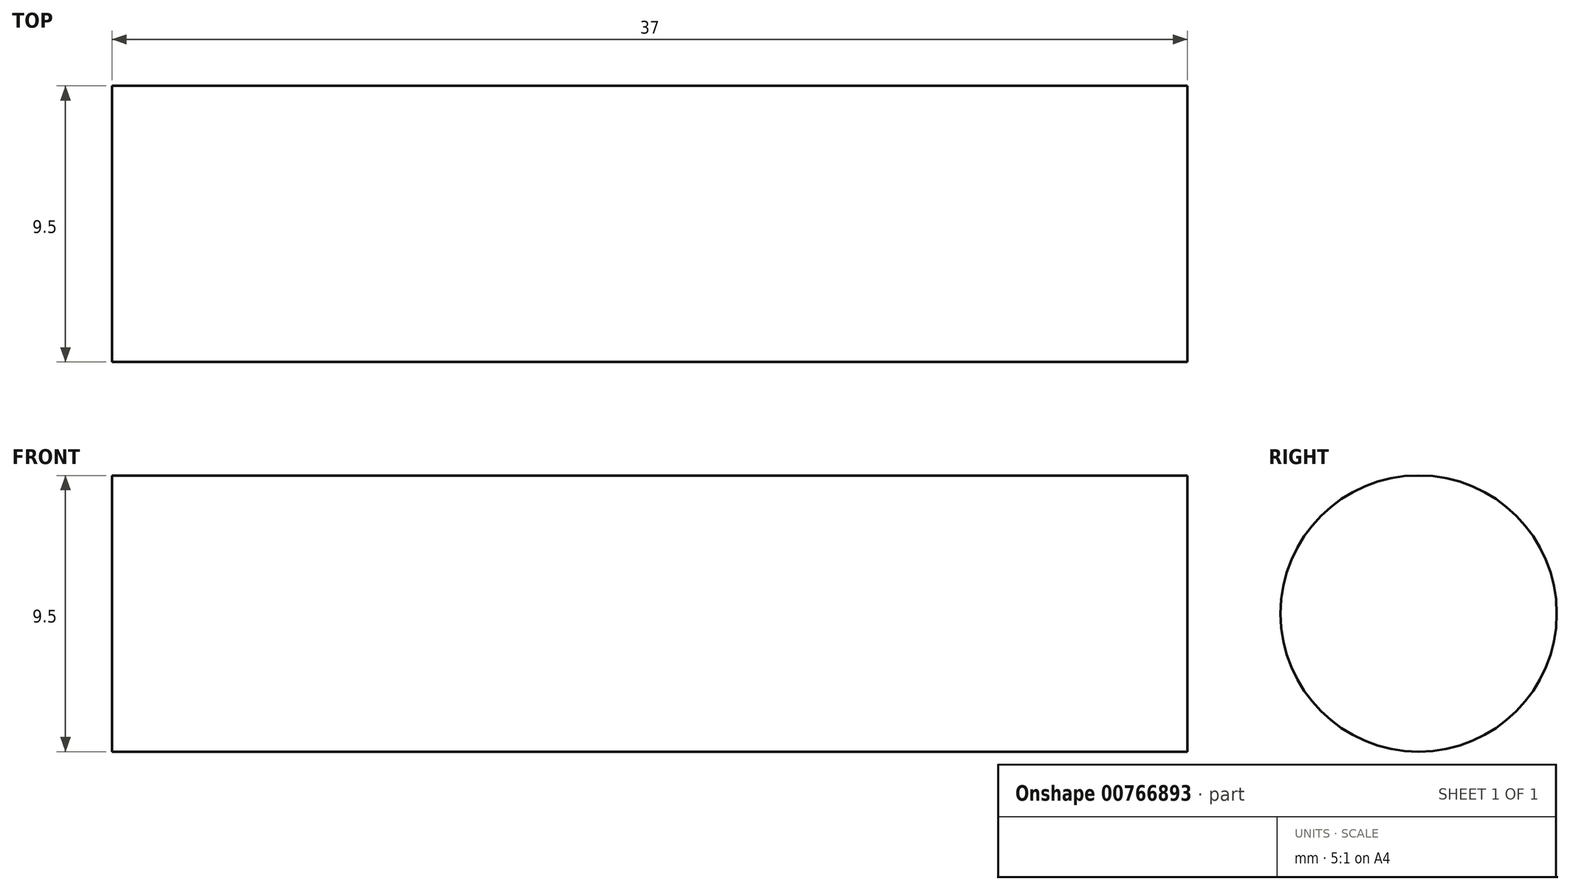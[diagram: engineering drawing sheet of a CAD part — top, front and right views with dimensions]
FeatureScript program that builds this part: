
annotation { "Feature Type Name" : "Feature", "Feature Type Description" : "" }
export const myFeature = defineFeature(function(context is Context, id is Id, definition is map)
    precondition{}
    {
        {
            var Q0;
            Q0=qCreatedBy(makeId("Right.planeOp"),FACE);
            var sketch = newSketch(context, id + "F0", { "sketchPlane" : qUnion([Q0])});
            skCircle(sketch, "E0", {"center": v(0, 0) * mm, "radius": 4.75 * mm});
            skSolve(sketch);
        }
        {
            var Q0;
            Q0=makeQuery(id+"F0.imprint","IMPRINT",FACE,{"disambiguationData":[TD([[makeQuery(id+"F0.imprint","IMPRINT",EDGE,{"derivedFrom":sQuery(id+"F0.wireOp",EDGE,"E0")}),1.0]])]});
            extrude(context, id + "F1", {"entities" : qUnion([Q0]), "depth" : 37 * mm, "offsetDistance" : 25 * mm});
        }
    });
